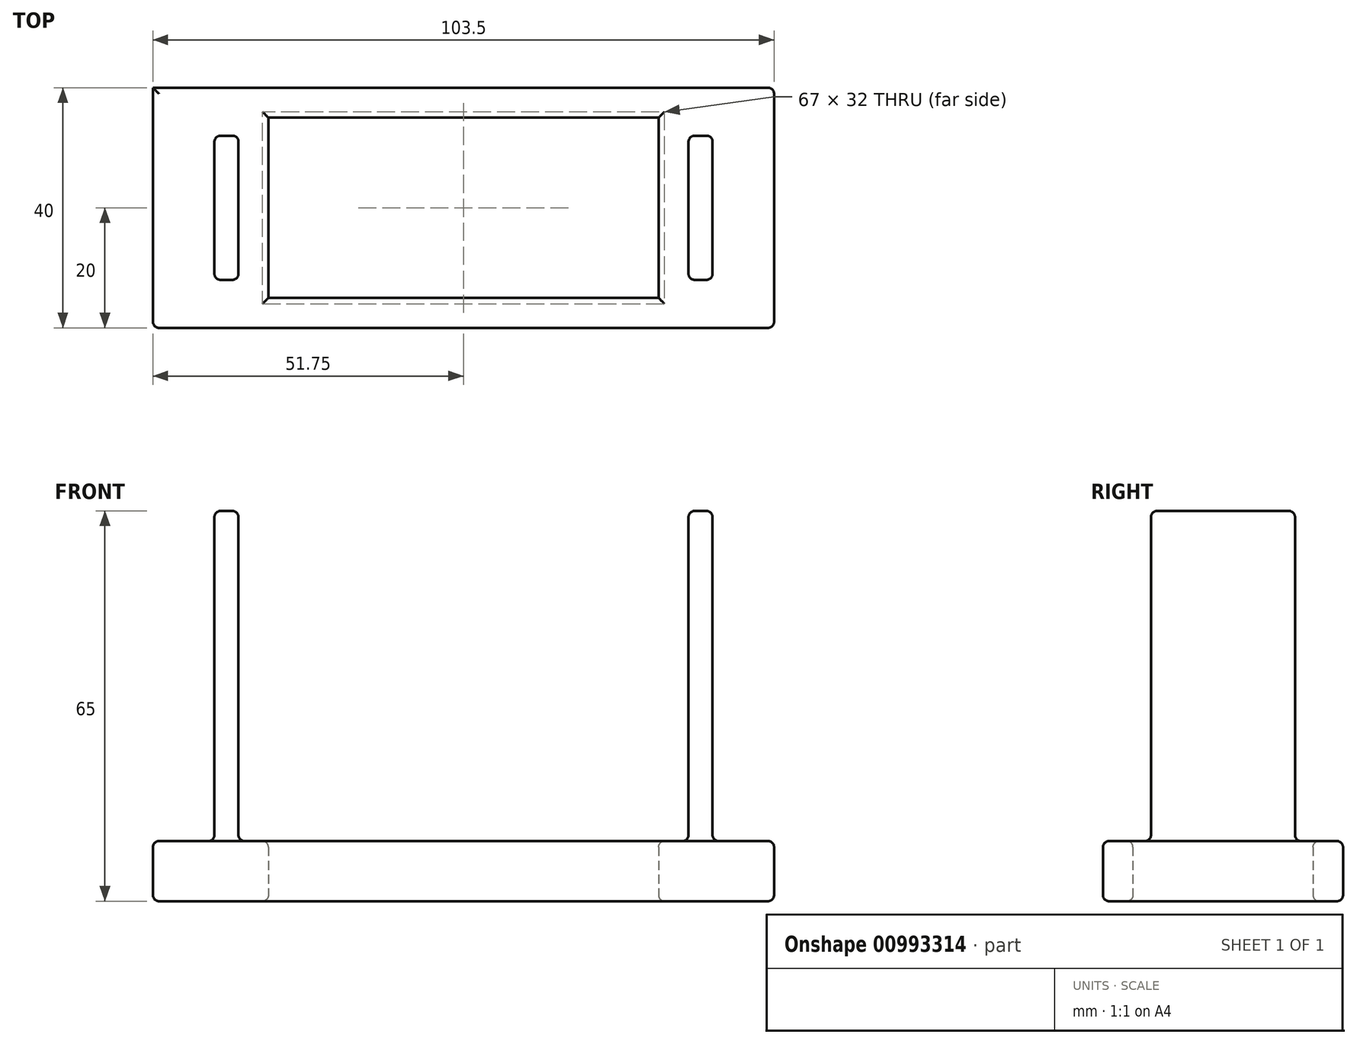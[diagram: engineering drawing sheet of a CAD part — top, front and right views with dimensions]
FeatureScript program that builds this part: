
annotation { "Feature Type Name" : "Feature", "Feature Type Description" : "" }
export const myFeature = defineFeature(function(context is Context, id is Id, definition is map)
    precondition{}
    {
        {
            var Q0;
            Q0=qCreatedBy(makeId("Top.planeOp"),FACE);
            var sketch = newSketch(context, id + "F0", { "sketchPlane" : qUnion([Q0])});
            skLineSegment(sketch, "E0.bottom", {"start": v(-51.75, 20) * mm, "end": v(51.75, 20) * mm});
            skLineSegment(sketch, "E0.top", {"start": v(-51.75, -20) * mm, "end": v(51.75, -20) * mm});
            skLineSegment(sketch, "E0.left", {"start": v(-51.75, 20) * mm, "end": v(-51.75, -20) * mm});
            skLineSegment(sketch, "E0.right", {"start": v(51.75, 20) * mm, "end": v(51.75, -20) * mm});
            skLineSegment(sketch, "E1", {"start": v(0, 0) * mm, "end": v(51.75, 0) * mm, "construction": true});
            skLineSegment(sketch, "E2", {"start": v(0, 0) * mm, "end": v(0, 20) * mm, "construction": true});
            skLineSegment(sketch, "E3.bottom", {"start": v(-32.5, -15) * mm, "end": v(32.5, -15) * mm});
            skLineSegment(sketch, "E3.top", {"start": v(-32.5, 15) * mm, "end": v(32.5, 15) * mm});
            skLineSegment(sketch, "E3.left", {"start": v(-32.5, -15) * mm, "end": v(-32.5, 15) * mm});
            skLineSegment(sketch, "E3.right", {"start": v(32.5, -15) * mm, "end": v(32.5, 15) * mm});
            skPoint(sketch, "E3.middle", {"position": v(0, 0) * mm});
            skLineSegment(sketch, "E4", {"start": v(0, 20) * mm, "end": v(0, -20) * mm, "construction": true});
            skLineSegment(sketch, "E5.bottom", {"start": v(-41.5, 12) * mm, "end": v(-37.5, 12) * mm});
            skLineSegment(sketch, "E5.top", {"start": v(-41.5, -12) * mm, "end": v(-37.5, -12) * mm});
            skLineSegment(sketch, "E5.left", {"start": v(-41.5, 12) * mm, "end": v(-41.5, -12) * mm});
            skLineSegment(sketch, "E5.right", {"start": v(-37.5, 12) * mm, "end": v(-37.5, -12) * mm});
            skPoint(sketch, "E6", {"position": v(-41.5, 0) * mm});
            skPoint(sketch, "E7", {"position": v(-51.75, 0) * mm});
            skLineSegment(sketch, "E8", {"start": v(-51.75, 0) * mm, "end": v(-41.5, 0) * mm, "construction": true});
            skLineSegment(sketch, "E9.MirrorCS", {"start": v(41.5, 12) * mm, "end": v(41.5, -12) * mm});
            skLineSegment(sketch, "E10.MirrorCS", {"start": v(37.5, 12) * mm, "end": v(37.5, -12) * mm});
            skLineSegment(sketch, "E11.MirrorCS", {"start": v(41.5, 12) * mm, "end": v(37.5, 12) * mm});
            skLineSegment(sketch, "E12.MirrorCS", {"start": v(41.5, -12) * mm, "end": v(37.5, -12) * mm});
            skLineSegment(sketch, "E13.MirrorCS", {"start": v(51.75, 0) * mm, "end": v(41.5, 0) * mm, "construction": true});
            skLineSegment(sketch, "E14", {"start": v(-37.5, 0) * mm, "end": v(0, 0) * mm});
            skSolve(sketch);
        }
        {
            var Q0;
            Q0=makeQuery(id+"F0.imprint","IMPRINT",FACE,{"disambiguationData":[TD([[makeQuery(id+"F0.imprint","IMPRINT",EDGE,{"derivedFrom":sQuery(id+"F0.wireOp",EDGE,"E0.bottom")}),-1.0]])]});
            extrude(context, id + "F1", {"entities" : qUnion([Q0]), "depth" : 10 * mm, "offsetDistance" : 25 * mm});
        }
        {
            var Q0;
            Q0=makeQuery(id+"F0.imprint","IMPRINT",FACE,{"disambiguationData":[TD([[makeQuery(id+"F0.imprint","IMPRINT",EDGE,{"derivedFrom":sQuery(id+"F0.wireOp",EDGE,"E5.bottom")}),-1.0]])]});
            extrude(context, id + "F2", {"entities" : qUnion([Q0]), "operationType" : NewBodyOperationType.ADD, "depth" : 65 * mm, "offsetDistance" : 25 * mm});
        }
        {
            var Q0;
            Q0=makeQuery(id+"F0.imprint","IMPRINT",FACE,{"disambiguationData":[TD([[makeQuery(id+"F0.imprint","IMPRINT",EDGE,{"derivedFrom":sQuery(id+"F0.wireOp",EDGE,"E9.MirrorCS")}),-1.0]])]});
            extrude(context, id + "F3", {"entities" : qUnion([Q0]), "operationType" : NewBodyOperationType.ADD, "depth" : 65 * mm, "offsetDistance" : 25 * mm});
        }
        {
            var Q0;
            Q0=makeQuery(id+"F1.opExtrude","SWEPT_FACE",FACE,{"disambiguationData":[OSD([sQuery(id+"F0.wireOp",EDGE,"E0.top")])]});
            var Q1;
            Q1=makeQuery(id+"F1.opExtrude","SWEPT_FACE",FACE,{"disambiguationData":[OSD([sQuery(id+"F0.wireOp",EDGE,"E0.right")])]});
            var Q2;
            Q2=makeQuery(id+"F1.opExtrude","CAP_FACE",FACE,{"disambiguationData":[OSD([sQuery(id+"F0.wireOp",EDGE,"E0.bottom"),sQuery(id+"F0.wireOp",EDGE,"E0.top"),sQuery(id+"F0.wireOp",EDGE,"E0.left"),sQuery(id+"F0.wireOp",EDGE,"E0.right"),sQuery(id+"F0.wireOp",EDGE,"E3.bottom"),sQuery(id+"F0.wireOp",EDGE,"E3.top"),sQuery(id+"F0.wireOp",EDGE,"E3.left"),sQuery(id+"F0.wireOp",EDGE,"E3.right"),sQuery(id+"F0.wireOp",EDGE,"E5.bottom"),sQuery(id+"F0.wireOp",EDGE,"E5.top"),sQuery(id+"F0.wireOp",EDGE,"E5.left"),sQuery(id+"F0.wireOp",EDGE,"E5.right"),sQuery(id+"F0.wireOp",EDGE,"E9.MirrorCS"),sQuery(id+"F0.wireOp",EDGE,"E10.MirrorCS"),sQuery(id+"F0.wireOp",EDGE,"E11.MirrorCS"),sQuery(id+"F0.wireOp",EDGE,"E12.MirrorCS")])],"isStart":false});
            var Q3;
            Q3=makeQuery(id+"F3.opExtrude","SWEPT_FACE",FACE,{"disambiguationData":[OSD([sQuery(id+"F0.wireOp",EDGE,"E11.MirrorCS")])]});
            var Q4;
            Q4=makeQuery(id+"F3.opExtrude","CAP_FACE",FACE,{"disambiguationData":[OSD([sQuery(id+"F0.wireOp",EDGE,"E9.MirrorCS"),sQuery(id+"F0.wireOp",EDGE,"E10.MirrorCS"),sQuery(id+"F0.wireOp",EDGE,"E11.MirrorCS"),sQuery(id+"F0.wireOp",EDGE,"E12.MirrorCS")])],"isStart":false});
            var Q5;
            Q5=makeQuery(id+"F2.opExtrude","SWEPT_FACE",FACE,{"disambiguationData":[OSD([sQuery(id+"F0.wireOp",EDGE,"E5.bottom")])]});
            var Q6;
            Q6=makeQuery(id+"F3.opExtrude","SWEPT_FACE",FACE,{"disambiguationData":[OSD([sQuery(id+"F0.wireOp",EDGE,"E9.MirrorCS")])]});
            var Q7;
            Q7=makeQuery(id+"F3.opExtrude","SWEPT_FACE",FACE,{"disambiguationData":[OSD([sQuery(id+"F0.wireOp",EDGE,"E12.MirrorCS")])]});
            var Q8;
            Q8=makeQuery(id+"F2.opExtrude","SWEPT_FACE",FACE,{"disambiguationData":[OSD([sQuery(id+"F0.wireOp",EDGE,"E5.right")])]});
            var Q9;
            Q9=makeQuery(id+"F2.opExtrude","SWEPT_FACE",FACE,{"disambiguationData":[OSD([sQuery(id+"F0.wireOp",EDGE,"E5.top")])]});
            var Q10;
            Q10=makeQuery(id+"F2.opExtrude","SWEPT_FACE",FACE,{"disambiguationData":[OSD([sQuery(id+"F0.wireOp",EDGE,"E5.left")])]});
            var Q11;
            {var subQ0=sQuery(id+"F0.wireOp",EDGE,"E12.MirrorCS");var subQ1=sQuery(id+"F0.wireOp",EDGE,"E11.MirrorCS");var subQ2=sQuery(id+"F0.wireOp",EDGE,"E10.MirrorCS");var subQ3=sQuery(id+"F0.wireOp",EDGE,"E9.MirrorCS");var subQ4=sQuery(id+"F0.wireOp",EDGE,"E5.right");var subQ5=sQuery(id+"F0.wireOp",EDGE,"E5.left");var subQ6=sQuery(id+"F0.wireOp",EDGE,"E5.top");var subQ7=sQuery(id+"F0.wireOp",EDGE,"E5.bottom");Q11=makeQuery(id+"F3.boolean.opBoolean","MERGE",FACE,{"derivedFrom":[makeQuery(id+"F2.boolean.opBoolean","MERGE",FACE,{"derivedFrom":[makeQuery(id+"F1.opExtrude","CAP_FACE",FACE,{"disambiguationData":[OSD([sQuery(id+"F0.wireOp",EDGE,"E0.bottom"),sQuery(id+"F0.wireOp",EDGE,"E0.top"),sQuery(id+"F0.wireOp",EDGE,"E0.left"),sQuery(id+"F0.wireOp",EDGE,"E0.right"),sQuery(id+"F0.wireOp",EDGE,"E3.bottom"),sQuery(id+"F0.wireOp",EDGE,"E3.top"),sQuery(id+"F0.wireOp",EDGE,"E3.left"),sQuery(id+"F0.wireOp",EDGE,"E3.right"),subQ7,subQ6,subQ5,subQ4,subQ3,subQ2,subQ1,subQ0])],"isStart":true}),makeQuery(id+"F2.opExtrude","CAP_FACE",FACE,{"disambiguationData":[OSD([subQ7,subQ6,subQ5,subQ4])],"isStart":true})]}),makeQuery(id+"F3.opExtrude","CAP_FACE",FACE,{"disambiguationData":[OSD([subQ3,subQ2,subQ1,subQ0])],"isStart":true})]});}
            fillet(context, id + "F4", {"entities" : qUnion([Q0, Q1, Q2, Q3, Q4, Q5, Q6, Q7, Q8, Q9, Q10, Q11]), "radius" : 1 * mm, "tangentPropagation" : true, "allowEdgeOverflow" : false});
        }
    });
